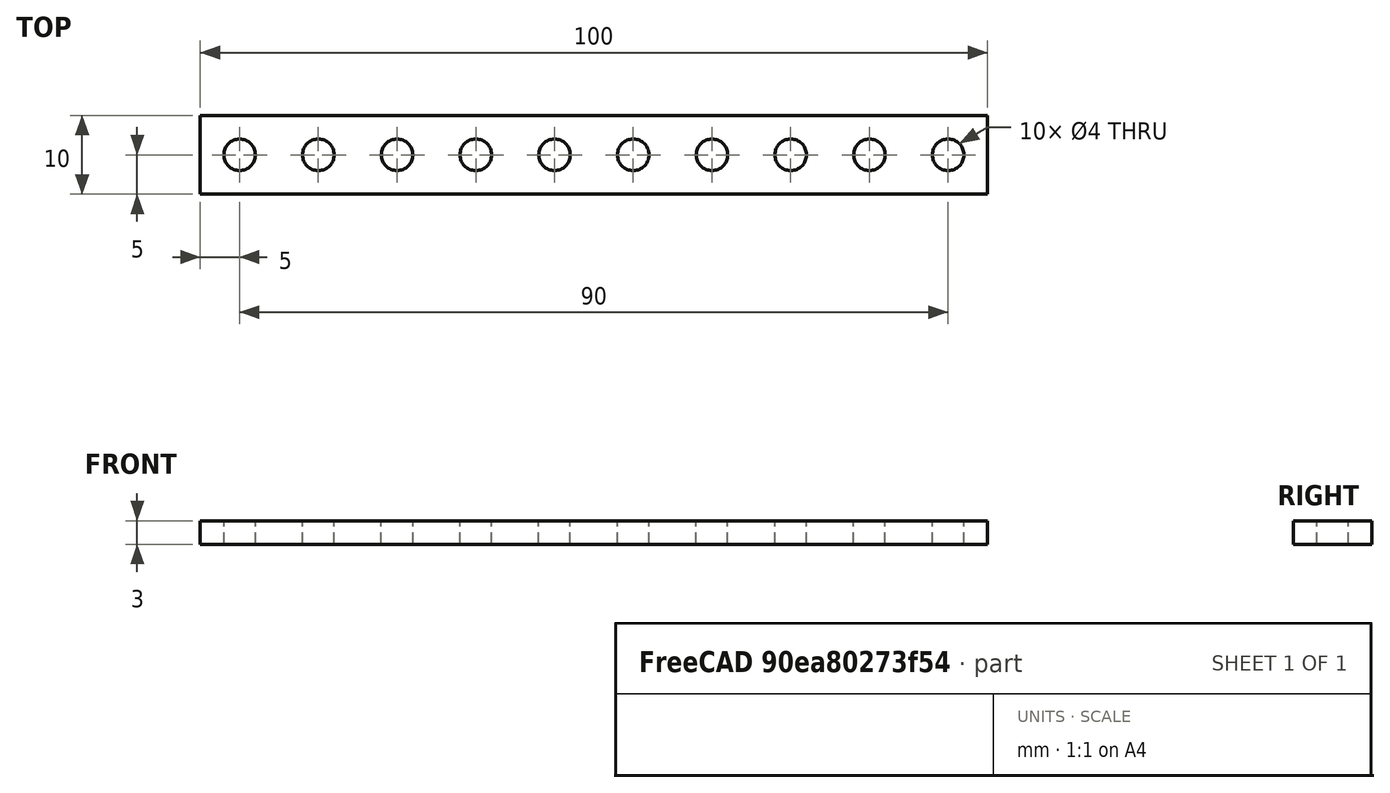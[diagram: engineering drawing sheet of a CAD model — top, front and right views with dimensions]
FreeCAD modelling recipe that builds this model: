
FCSTD DOCUMENT  (FreeCAD 0.16R6707 (Git))
Label: 04-pieza-mecano-2
License: All rights reserved
LicenseURL: http://en.wikipedia.org/wiki/All_rights_reserved
objects: Part::Box×1, Part::Cylinder×1, Part::Cut×1, Part::FeaturePython×1
note: 4 computed .brp shape members not serialized (recipe doc carries the construction recipe); baked Part::Feature solids carry a one-line shape summary decoded from their .brp

FEATURE [Part::Box] Box  label="Cubo"
  Height = 3
  Length = 10
  Width = 10
FEATURE [Part::Cylinder] Cylinder  label="Cilindro"
  Angle = 360
  Height = 10
  Placement = pos=(5,5,-3) rot=(0,0,1;0rad)
  Radius = 2
FEATURE [Part::Cut] Cut  label="pieza-unitaria"
  Base = -> Box
  Tool = -> Cylinder
FEATURE [Part::FeaturePython] Array  label="Pieza-mecano"  # Draft array (typed FeaturePython)
  Angle = 360
  ArrayType = 0
  Axis = (0,0,1)
  Base = -> Cut
  Center = (0,0,0)
  Fuse = true
  IntervalAxis = (0,0,0)
  IntervalX = (10,0,0)
  IntervalY = (0,1,0)
  IntervalZ = (0,0,0)
  NumberPolar = 1
  NumberX = 10
  NumberY = 1
  NumberZ = 1
